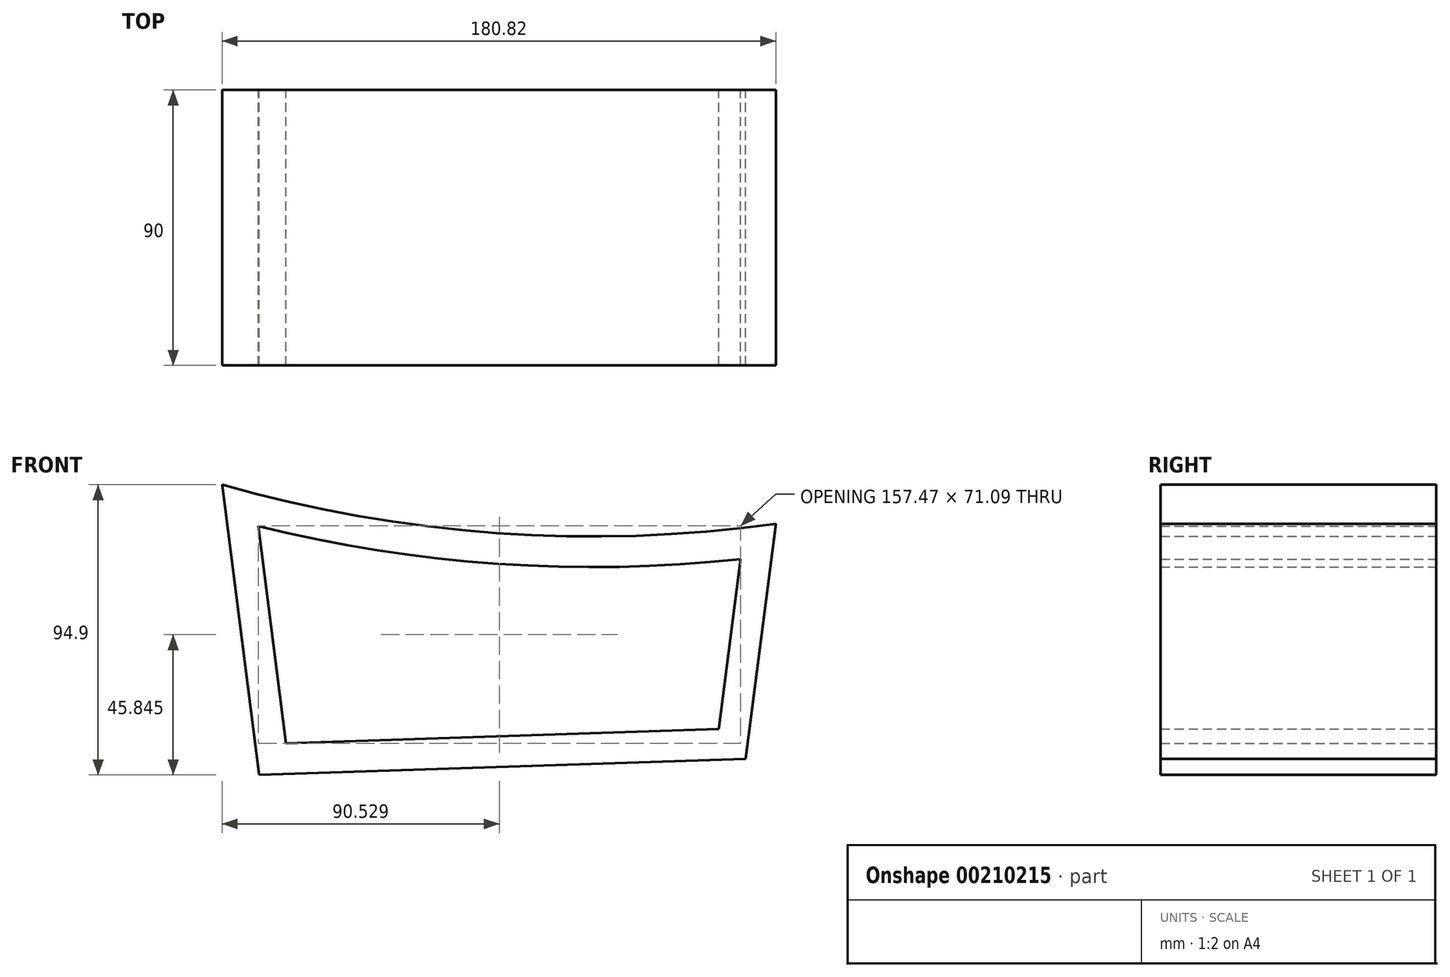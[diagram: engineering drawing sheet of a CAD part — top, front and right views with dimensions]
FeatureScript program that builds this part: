
annotation { "Feature Type Name" : "Feature", "Feature Type Description" : "" }
export const myFeature = defineFeature(function(context is Context, id is Id, definition is map)
    precondition{}
    {
        {
            var Q0;
            Q0=qCreatedBy(makeId("Front.planeOp"),FACE);
            var sketch = newSketch(context, id + "F0", { "sketchPlane" : qUnion([Q0])});
            skArc(sketch, "E0", {"start": v(0, 88.48) * mm, "mid": v(89.75, 72.65) * mm, "end": v(180.83, 75.65) * mm});
            skLineSegment(sketch, "E1", {"start": v(0, 88.48) * mm, "end": v(11.44, -1.44) * mm});
            skLineSegment(sketch, "E2", {"start": v(11.44, -1.44) * mm, "end": v(11.44, -1.44) * mm});
            skLineSegment(sketch, "E3", {"start": v(12.08, -6.42) * mm, "end": v(171, -1.1) * mm});
            skLineSegment(sketch, "E4", {"start": v(180.83, 75.65) * mm, "end": v(171, -1.1) * mm});
            skLineSegment(sketch, "E5.0", {"start": v(169.27, 64.16) * mm, "end": v(162.16, 8.6) * mm});
            skArc(sketch, "E5.1", {"start": v(11.8, 74.97) * mm, "mid": v(90.06, 62.6) * mm, "end": v(169.27, 64.16) * mm});
            skLineSegment(sketch, "E5.2", {"start": v(11.8, 74.97) * mm, "end": v(20.85, 3.88) * mm});
            skLineSegment(sketch, "E5.3", {"start": v(20.85, 3.88) * mm, "end": v(162.16, 8.6) * mm});
            skLineSegment(sketch, "E6", {"start": v(12.08, -6.42) * mm, "end": v(11.44, -1.44) * mm});
            skSolve(sketch);
        }
        {
            var Q0;
            Q0 = qSketchRegion(id + "F0", true);
            extrude(context, id + "F1", {"entities" : qUnion([Q0]), "endBound" : BoundingType.SYMMETRIC, "depth" : 90 * mm});
        }
    });
